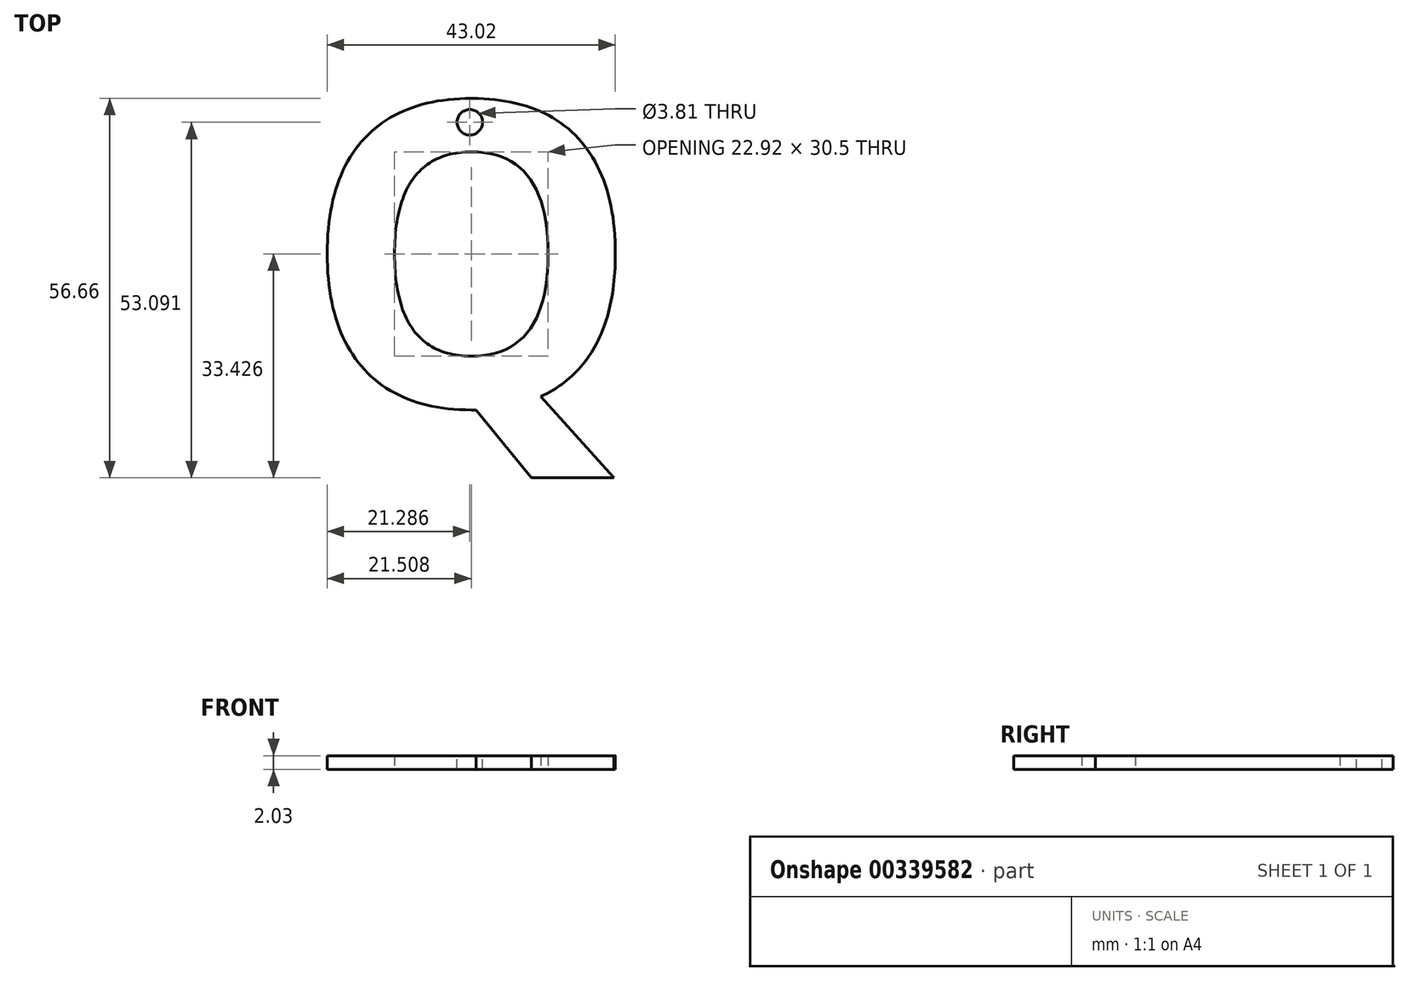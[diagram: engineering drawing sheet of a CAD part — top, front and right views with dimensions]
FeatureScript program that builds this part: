
annotation { "Feature Type Name" : "Feature", "Feature Type Description" : "" }
export const myFeature = defineFeature(function(context is Context, id is Id, definition is map)
    precondition{}
    {
        {
            var Q0;
            Q0=qCreatedBy(makeId("Top.planeOp"),FACE);
            var sketch = newSketch(context, id + "F0", { "sketchPlane" : qUnion([Q0])});
            skText(sketch, "E0", { "text": "Q", "fontName": "OpenSans-Bold.ttf"});
            const initialGuessF0  = {"E0": [-0.02278, -0.0235, 1, 0, 0.04557]};
            skSetInitialGuess(sketch, initialGuessF0);
            skSolve(sketch);
        }
        {
            var Q0;
            Q0 = qSketchRegion(id + "F0", true);
            extrude(context, id + "F1", {"entities" : qUnion([Q0]), "depth" : 2.03 * mm});
        }
        {
            var Q0;
            Q0=makeQuery(id+"F1.opExtrude","CAP_FACE",FACE,{"disambiguationData":[OSD([sQuery(id+"F0.wireOp",EDGE,"E0.sketch_text.stroke-0"),sQuery(id+"F0.wireOp",EDGE,"E0.sketch_text.stroke-1"),sQuery(id+"F0.wireOp",EDGE,"E0.sketch_text.stroke-2"),sQuery(id+"F0.wireOp",EDGE,"E0.sketch_text.stroke-3"),sQuery(id+"F0.wireOp",EDGE,"E0.sketch_text.stroke-4"),sQuery(id+"F0.wireOp",EDGE,"E0.sketch_text.stroke-5"),sQuery(id+"F0.wireOp",EDGE,"E0.sketch_text.stroke-6"),sQuery(id+"F0.wireOp",EDGE,"E0.sketch_text.stroke-7"),sQuery(id+"F0.wireOp",EDGE,"E0.sketch_text.stroke-8"),sQuery(id+"F0.wireOp",EDGE,"E0.sketch_text.stroke-9"),sQuery(id+"F0.wireOp",EDGE,"E0.sketch_text.stroke-10"),sQuery(id+"F0.wireOp",EDGE,"E0.sketch_text.stroke-11"),sQuery(id+"F0.wireOp",EDGE,"E0.sketch_text.stroke-12"),sQuery(id+"F0.wireOp",EDGE,"E0.sketch_text.stroke-13"),sQuery(id+"F0.wireOp",EDGE,"E0.sketch_text.stroke-14"),sQuery(id+"F0.wireOp",EDGE,"E0.sketch_text.stroke-15"),sQuery(id+"F0.wireOp",EDGE,"E0.sketch_text.stroke-16"),sQuery(id+"F0.wireOp",EDGE,"E0.sketch_text.stroke-17")])],"isStart":false});
            var sketch = newSketch(context, id + "F2", { "sketchPlane" : qUnion([Q0])});
            skCircle(sketch, "E1", {"center": v(2.19, 18.83) * mm, "radius": 1.9 * mm});
            skSolve(sketch);
        }
        {
            var Q0;
            Q0 = qSketchRegion(id + "F2", true);
            extrude(context, id + "F3", {"entities" : qUnion([Q0]), "operationType" : NewBodyOperationType.REMOVE, "endBound" : BoundingType.THROUGH_ALL, "oppositeDirection" : true, "depth" : 25.4 * mm});
        }
    });
